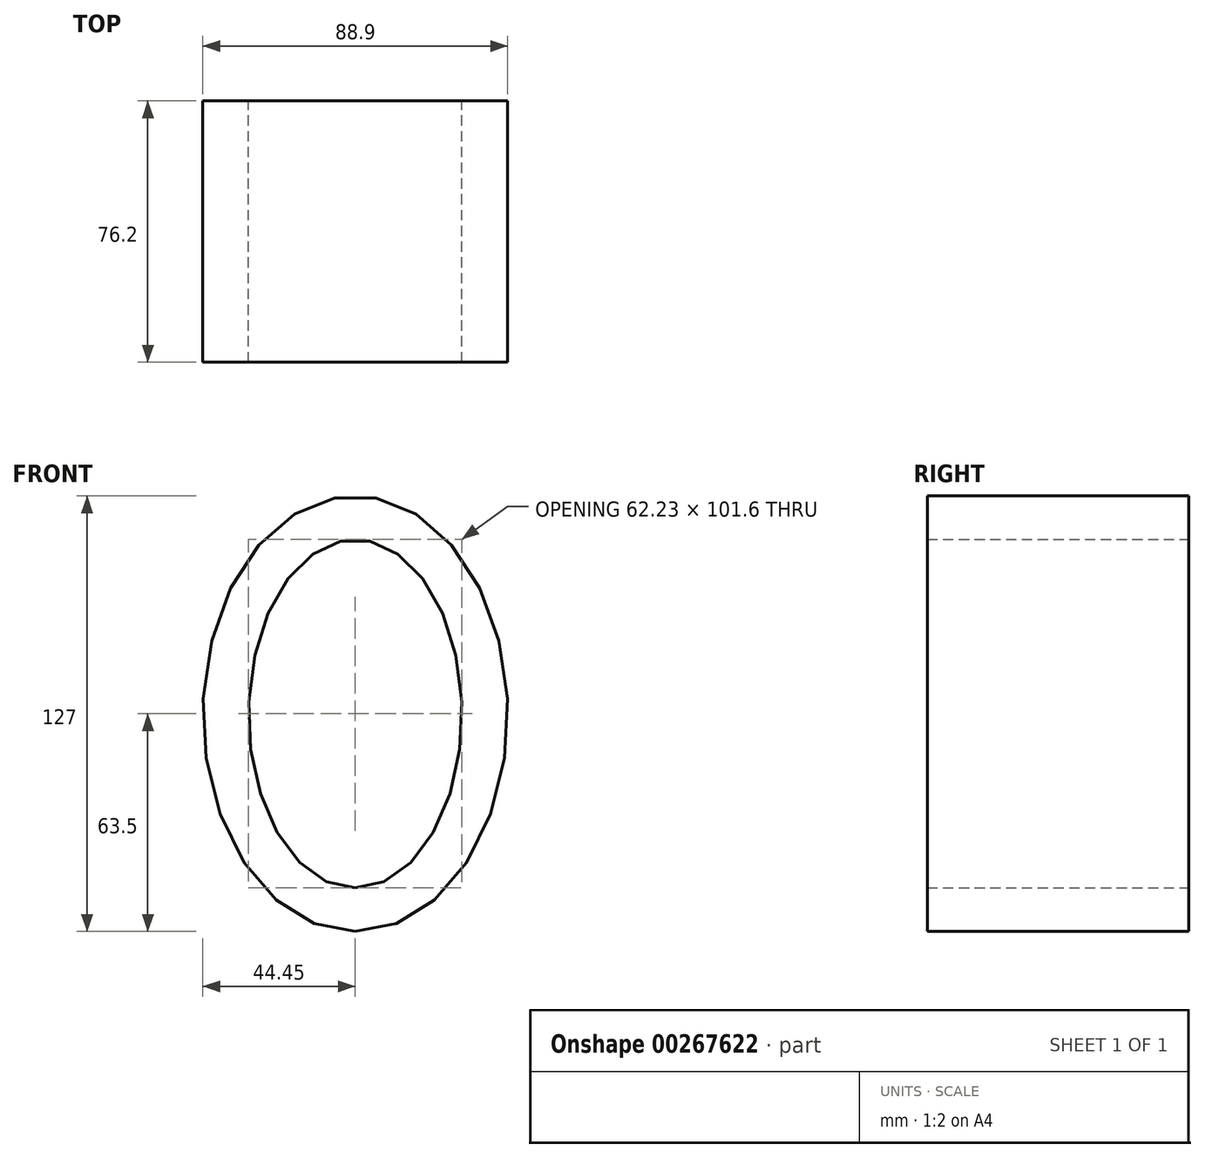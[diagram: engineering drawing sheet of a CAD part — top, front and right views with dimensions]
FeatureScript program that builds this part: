
annotation { "Feature Type Name" : "Feature", "Feature Type Description" : "" }
export const myFeature = defineFeature(function(context is Context, id is Id, definition is map)
    precondition{}
    {
        {
            var Q0;
            Q0=qCreatedBy(makeId("Front.planeOp"),FACE);
            var sketch = newSketch(context, id + "F0", { "sketchPlane" : qUnion([Q0])});
            skEllipse(sketch, "E0", {"center": v(0, 0) * mm, "majorRadius": 63.5 * mm, "minorRadius": 44.45 * mm, "majorAxis": v(0, -1)});
            skEllipse(sketch, "E1", {"center": v(0, 0) * mm, "majorRadius": 50.8 * mm, "minorRadius": 31.12 * mm, "majorAxis": v(0, -1)});
            skSolve(sketch);
        }
        {
            var Q0;
            Q0=makeQuery(id+"F0.imprint","IMPRINT",FACE,{"disambiguationData":[TD([[makeQuery(id+"F0.imprint","IMPRINT",EDGE,{"derivedFrom":sQuery(id+"F0.wireOp",EDGE,"E0")}),1.0]])]});
            extrude(context, id + "F1", {"entities" : qUnion([Q0]), "depth" : 76.2 * mm});
        }
    });
